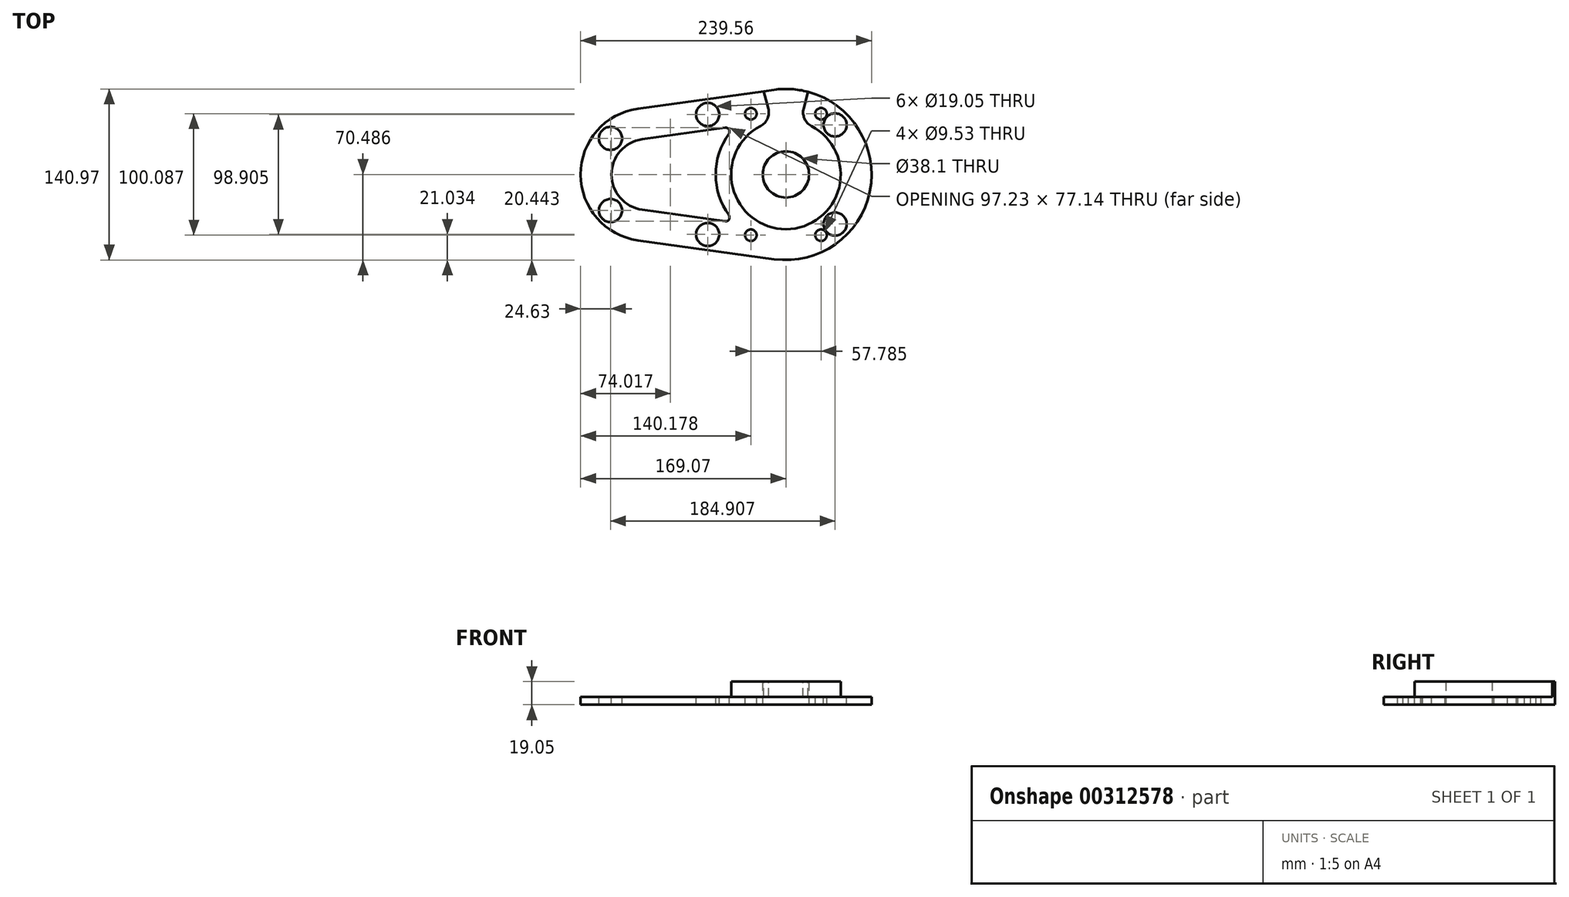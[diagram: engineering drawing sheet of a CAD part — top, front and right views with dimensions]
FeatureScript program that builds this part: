
annotation { "Feature Type Name" : "Feature", "Feature Type Description" : "" }
export const myFeature = defineFeature(function(context is Context, id is Id, definition is map)
    precondition{}
    {
        {
            var Q0;
            Q0=qCreatedBy(makeId("Top.planeOp"),FACE);
            var sketch = newSketch(context, id + "F0", { "sketchPlane" : qUnion([Q0])});
            skLineSegment(sketch, "E0", {"start": v(145.58, -278.48) * mm, "end": v(-159.22, -278.48) * mm});
            skLineSegment(sketch, "E1", {"start": v(-159.22, -278.48) * mm, "end": v(-159.22, -532.48) * mm});
            skLineSegment(sketch, "E2", {"start": v(-159.22, -532.48) * mm, "end": v(145.58, -532.48) * mm});
            skLineSegment(sketch, "E3", {"start": v(145.58, -278.48) * mm, "end": v(145.58, -532.48) * mm});
            skLineSegment(sketch, "E4", {"start": v(145.58, -11.78) * mm, "end": v(145.58, -265.78) * mm});
            skLineSegment(sketch, "E5", {"start": v(-159.22, -265.78) * mm, "end": v(145.58, -265.78) * mm});
            skLineSegment(sketch, "E6", {"start": v(-159.22, -11.78) * mm, "end": v(-159.22, -265.78) * mm});
            skLineSegment(sketch, "E7", {"start": v(145.58, -11.78) * mm, "end": v(-159.22, -11.78) * mm});
            skLineSegment(sketch, "E8", {"start": v(145.58, 254.92) * mm, "end": v(145.58, 0.92) * mm});
            skLineSegment(sketch, "E9", {"start": v(-159.22, 0.92) * mm, "end": v(145.58, 0.92) * mm});
            skLineSegment(sketch, "E10", {"start": v(-159.22, 254.92) * mm, "end": v(-159.22, 0.92) * mm});
            skLineSegment(sketch, "E11", {"start": v(145.58, 254.92) * mm, "end": v(-159.22, 254.92) * mm});
            skLineSegment(sketch, "E12", {"start": v(-79.36, -351.24) * mm, "end": v(32.78, -335.67) * mm});
            skArc(sketch, "E13", {"start": v(32.78, -335.67) * mm, "mid": v(112.96, -405.48) * mm, "end": v(32.78, -475.3) * mm});
            skLineSegment(sketch, "E14", {"start": v(32.78, -475.3) * mm, "end": v(-79.36, -459.73) * mm});
            skArc(sketch, "E15", {"start": v(-79.36, -459.73) * mm, "mid": v(-126.6, -405.48) * mm, "end": v(-79.36, -351.24) * mm});
            skArc(sketch, "E16", {"start": v(-75.87, -434.57) * mm, "mid": v(-101.2, -405.48) * mm, "end": v(-75.87, -376.4) * mm});
            skLineSegment(sketch, "E17", {"start": v(-75.87, -376.4) * mm, "end": v(-7.58, -366.91) * mm});
            skArc(sketch, "E18", {"start": v(-7.58, -366.91) * mm, "mid": v(-4.42, -368.41) * mm, "end": v(-4.56, -371.9) * mm});
            skArc(sketch, "E19", {"start": v(-4.56, -371.9) * mm, "mid": v(-15.31, -405.48) * mm, "end": v(-4.56, -439.06) * mm});
            skArc(sketch, "E20", {"start": v(-4.56, -439.06) * mm, "mid": v(-4.42, -442.55) * mm, "end": v(-7.58, -444.05) * mm});
            skLineSegment(sketch, "E21", {"start": v(-7.58, -444.05) * mm, "end": v(-75.87, -434.57) * mm});
            skArc(sketch, "E22", {"start": v(-36.82, 333.52) * mm, "mid": v(-66.33, 359.53) * mm, "end": v(-77.3, 397.3) * mm});
            skArc(sketch, "E23", {"start": v(-77.3, 397.3) * mm, "mid": v(-73.32, 420.67) * mm, "end": v(-61.81, 441.4) * mm});
            skArc(sketch, "E24", {"start": v(-61.81, 441.4) * mm, "mid": v(-58.7, 447) * mm, "end": v(-57.62, 453.32) * mm});
            skLineSegment(sketch, "E25", {"start": v(-57.62, 453.32) * mm, "end": v(-57.62, 486.2) * mm});
            skLineSegment(sketch, "E26", {"start": v(-57.62, 486.2) * mm, "end": v(43.98, 486.2) * mm});
            skLineSegment(sketch, "E27", {"start": v(43.98, 486.2) * mm, "end": v(43.98, 453.32) * mm});
            skArc(sketch, "E28", {"start": v(43.98, 453.32) * mm, "mid": v(45.06, 447) * mm, "end": v(48.17, 441.4) * mm});
            skArc(sketch, "E29", {"start": v(48.17, 441.4) * mm, "mid": v(59.68, 420.67) * mm, "end": v(63.66, 397.3) * mm});
            skArc(sketch, "E30", {"start": v(63.66, 397.3) * mm, "mid": v(52.69, 359.53) * mm, "end": v(23.17, 333.52) * mm});
            skArc(sketch, "E31", {"start": v(23.17, 333.52) * mm, "mid": v(15.2, 326.49) * mm, "end": v(12.23, 316.28) * mm});
            skLineSegment(sketch, "E32", {"start": v(12.23, 316.28) * mm, "end": v(12.23, 302.05) * mm});
            skArc(sketch, "E33", {"start": v(12.23, 302.05) * mm, "mid": v(10.37, 297.56) * mm, "end": v(5.88, 295.7) * mm});
            skLineSegment(sketch, "E34", {"start": v(5.88, 295.7) * mm, "end": v(-3.65, 295.7) * mm});
            skLineSegment(sketch, "E35", {"start": v(-3.65, 295.7) * mm, "end": v(-3.65, 352.33) * mm});
            skArc(sketch, "E36", {"start": v(-3.65, 352.33) * mm, "mid": v(7.85, 354.67) * mm, "end": v(18.36, 359.9) * mm});
            skArc(sketch, "E37", {"start": v(18.36, 359.9) * mm, "mid": v(20.05, 360.44) * mm, "end": v(21.77, 359.99) * mm});
            skArc(sketch, "E38", {"start": v(21.77, 359.99) * mm, "mid": v(29.55, 360.93) * mm, "end": v(30.5, 368.7) * mm});
            skArc(sketch, "E39", {"start": v(30.5, 368.7) * mm, "mid": v(30.04, 370.43) * mm, "end": v(30.58, 372.12) * mm});
            skArc(sketch, "E40", {"start": v(30.58, 372.12) * mm, "mid": v(38.26, 397.3) * mm, "end": v(30.58, 422.48) * mm});
            skArc(sketch, "E41", {"start": v(30.58, 422.48) * mm, "mid": v(30.04, 424.18) * mm, "end": v(30.5, 425.9) * mm});
            skArc(sketch, "E42", {"start": v(30.5, 425.9) * mm, "mid": v(29.55, 433.67) * mm, "end": v(21.77, 434.62) * mm});
            skArc(sketch, "E43", {"start": v(21.77, 434.62) * mm, "mid": v(20.05, 434.16) * mm, "end": v(18.36, 434.7) * mm});
            skArc(sketch, "E44", {"start": v(18.36, 434.7) * mm, "mid": v(-6.82, 442.39) * mm, "end": v(-32, 434.7) * mm});
            skArc(sketch, "E45", {"start": v(-32, 434.7) * mm, "mid": v(-33.7, 434.16) * mm, "end": v(-35.42, 434.62) * mm});
            skArc(sketch, "E46", {"start": v(-35.42, 434.62) * mm, "mid": v(-43.2, 433.67) * mm, "end": v(-44.14, 425.9) * mm});
            skArc(sketch, "E47", {"start": v(-44.14, 425.9) * mm, "mid": v(-43.68, 424.18) * mm, "end": v(-44.22, 422.48) * mm});
            skArc(sketch, "E48", {"start": v(-44.22, 422.48) * mm, "mid": v(-51.9, 397.3) * mm, "end": v(-44.22, 372.12) * mm});
            skArc(sketch, "E49", {"start": v(-44.22, 372.12) * mm, "mid": v(-43.68, 370.43) * mm, "end": v(-44.14, 368.7) * mm});
            skArc(sketch, "E50", {"start": v(-44.14, 368.7) * mm, "mid": v(-43.2, 360.93) * mm, "end": v(-35.42, 359.99) * mm});
            skArc(sketch, "E51", {"start": v(-35.42, 359.99) * mm, "mid": v(-33.7, 360.44) * mm, "end": v(-32, 359.9) * mm});
            skArc(sketch, "E52", {"start": v(-32, 359.9) * mm, "mid": v(-21.5, 354.67) * mm, "end": v(-10, 352.33) * mm});
            skLineSegment(sketch, "E53", {"start": v(-10, 352.33) * mm, "end": v(-10, 295.7) * mm});
            skLineSegment(sketch, "E54", {"start": v(-10, 295.7) * mm, "end": v(-19.52, 295.7) * mm});
            skArc(sketch, "E55", {"start": v(-19.52, 295.7) * mm, "mid": v(-24.01, 297.56) * mm, "end": v(-25.87, 302.05) * mm});
            skLineSegment(sketch, "E56", {"start": v(-25.87, 302.05) * mm, "end": v(-25.87, 316.28) * mm});
            skArc(sketch, "E57", {"start": v(-25.87, 316.28) * mm, "mid": v(-28.84, 326.49) * mm, "end": v(-36.82, 333.52) * mm});
            skLineSegment(sketch, "E58", {"start": v(-46.03, -68.97) * mm, "end": v(66.11, -84.54) * mm});
            skArc(sketch, "E59", {"start": v(66.11, -84.54) * mm, "mid": v(113.35, -138.78) * mm, "end": v(66.11, -193.03) * mm});
            skLineSegment(sketch, "E60", {"start": v(66.11, -193.03) * mm, "end": v(-46.03, -208.6) * mm});
            skArc(sketch, "E61", {"start": v(-46.03, -208.6) * mm, "mid": v(-126.2, -138.78) * mm, "end": v(-46.03, -68.97) * mm});
            skArc(sketch, "E62", {"start": v(63.42, -365.56) * mm, "mid": v(57.7, -359.41) * mm, "end": v(57.06, -351.03) * mm});
            skLineSegment(sketch, "E63", {"start": v(57.06, -351.03) * mm, "end": v(60.71, -337.4) * mm});
            skArc(sketch, "E64", {"start": v(60.71, -337.4) * mm, "mid": v(46.83, -335.13) * mm, "end": v(32.78, -335.67) * mm});
            skLineSegment(sketch, "E65", {"start": v(32.78, -335.67) * mm, "end": v(24.09, -336.87) * mm});
            skLineSegment(sketch, "E66", {"start": v(24.09, -336.87) * mm, "end": v(27.88, -351.03) * mm});
            skArc(sketch, "E67", {"start": v(27.88, -351.03) * mm, "mid": v(27.25, -359.41) * mm, "end": v(21.52, -365.56) * mm});
            skArc(sketch, "E68", {"start": v(21.52, -365.56) * mm, "mid": v(42.47, -450.57) * mm, "end": v(63.42, -365.56) * mm});
            skCircle(sketch, "E69", {"center": v(58.58, -138.78) * mm, "radius": 29.37 * mm});
            skCircle(sketch, "E70", {"center": v(42.47, -405.48) * mm, "radius": 19.05 * mm});
            skCircle(sketch, "E71", {"center": v(88.33, -109.04) * mm, "radius": 9.53 * mm});
            skCircle(sketch, "E72", {"center": v(8.3, -89.33) * mm, "radius": 9.53 * mm});
            skCircle(sketch, "E73", {"center": v(8.3, -188.24) * mm, "radius": 9.53 * mm});
            skCircle(sketch, "E74", {"center": v(-96.58, -97.92) * mm, "radius": 9.53 * mm});
            skCircle(sketch, "E75", {"center": v(-55.72, -138.78) * mm, "radius": 46.04 * mm});
            skCircle(sketch, "E76", {"center": v(88.33, -168.53) * mm, "radius": 9.53 * mm});
            skCircle(sketch, "E77", {"center": v(-96.58, -179.64) * mm, "radius": 9.53 * mm});
            skCircle(sketch, "E78", {"center": v(82.94, -364.62) * mm, "radius": 9.53 * mm});
            skCircle(sketch, "E79", {"center": v(-21.94, -356.03) * mm, "radius": 9.53 * mm});
            skCircle(sketch, "E80", {"center": v(-101.97, -375.74) * mm, "radius": 9.53 * mm});
            skCircle(sketch, "E81", {"center": v(-101.97, -435.23) * mm, "radius": 9.53 * mm});
            skCircle(sketch, "E82", {"center": v(-21.94, -454.94) * mm, "radius": 9.53 * mm});
            skCircle(sketch, "E83", {"center": v(82.94, -446.34) * mm, "radius": 9.53 * mm});
            skCircle(sketch, "E84", {"center": v(50.96, 397.3) * mm, "radius": 4.76 * mm});
            skCircle(sketch, "E85", {"center": v(-64.6, 397.3) * mm, "radius": 4.76 * mm});
            skCircle(sketch, "E86", {"center": v(71.36, -355.44) * mm, "radius": 4.76 * mm});
            skCircle(sketch, "E87", {"center": v(13.58, -455.53) * mm, "radius": 4.76 * mm});
            skCircle(sketch, "E88", {"center": v(13.58, -355.44) * mm, "radius": 4.76 * mm});
            skCircle(sketch, "E89", {"center": v(71.36, -455.53) * mm, "radius": 4.76 * mm});
            skCircle(sketch, "E90", {"center": v(-6.82, 127.92) * mm, "radius": 46.04 * mm});
            skCircle(sketch, "E91", {"center": v(-35.71, 77.87) * mm, "radius": 4.76 * mm});
            skCircle(sketch, "E92", {"center": v(22.07, 177.96) * mm, "radius": 4.76 * mm});
            skCircle(sketch, "E93", {"center": v(22.07, 77.87) * mm, "radius": 4.76 * mm});
            skCircle(sketch, "E94", {"center": v(-35.71, 177.96) * mm, "radius": 4.76 * mm});
            skCircle(sketch, "E95", {"center": v(-6.82, 127.92) * mm, "radius": 70.48 * mm});
            skCircle(sketch, "E96", {"center": v(-26.83, -88.74) * mm, "radius": 3.18 * mm});
            skCircle(sketch, "E97", {"center": v(-84.61, -88.74) * mm, "radius": 3.18 * mm});
            skCircle(sketch, "E98", {"center": v(-84.61, -188.83) * mm, "radius": 3.18 * mm});
            skCircle(sketch, "E99", {"center": v(-26.83, -188.83) * mm, "radius": 3.18 * mm});
            skSolve(sketch);
        }
        {
            var Q0;
            Q0=makeQuery(id+"F0.imprint","IMPRINT",FACE,{"disambiguationData":[TD([[makeQuery(id+"F0.imprint","IMPRINT",EDGE,{"derivedFrom":sQuery(id+"F0.wireOp",EDGE,"E12")}),-1.0]])]});
            var Q1;
            Q1=makeQuery(id+"F0.imprint","IMPRINT",FACE,{"disambiguationData":[TD([[makeQuery(id+"F0.imprint","IMPRINT",EDGE,{"derivedFrom":sQuery(id+"F0.wireOp",EDGE,"E62")}),1.0]])]});
            var Q2;
            Q2=makeQuery(id+"F0.imprint","IMPRINT",FACE,{"disambiguationData":[TD([[makeQuery(id+"F0.imprint","IMPRINT",EDGE,{"derivedFrom":sQuery(id+"F0.wireOp",EDGE,"E81")}),-1.0]])]});
            var Q3;
            Q3=makeQuery(id+"F0.imprint","IMPRINT",FACE,{"disambiguationData":[TD([[makeQuery(id+"F0.imprint","IMPRINT",EDGE,{"derivedFrom":sQuery(id+"F0.wireOp",EDGE,"E80")}),-1.0]])]});
            var Q4;
            Q4=makeQuery(id+"F0.imprint","IMPRINT",FACE,{"disambiguationData":[TD([[makeQuery(id+"F0.imprint","IMPRINT",EDGE,{"derivedFrom":sQuery(id+"F0.wireOp",EDGE,"E79")}),-1.0]])]});
            var Q5;
            Q5=makeQuery(id+"F0.imprint","IMPRINT",FACE,{"disambiguationData":[TD([[makeQuery(id+"F0.imprint","IMPRINT",EDGE,{"derivedFrom":sQuery(id+"F0.wireOp",EDGE,"E78")}),-1.0]])]});
            var Q6;
            Q6=makeQuery(id+"F0.imprint","IMPRINT",FACE,{"disambiguationData":[TD([[makeQuery(id+"F0.imprint","IMPRINT",EDGE,{"derivedFrom":sQuery(id+"F0.wireOp",EDGE,"E83")}),-1.0]])]});
            var Q7;
            Q7=makeQuery(id+"F0.imprint","IMPRINT",FACE,{"disambiguationData":[TD([[makeQuery(id+"F0.imprint","IMPRINT",EDGE,{"derivedFrom":sQuery(id+"F0.wireOp",EDGE,"E82")}),-1.0]])]});
            var Q8;
            Q8=makeQuery(id+"F0.imprint","IMPRINT",FACE,{"disambiguationData":[TD([[makeQuery(id+"F0.imprint","IMPRINT",EDGE,{"derivedFrom":sQuery(id+"F0.wireOp",EDGE,"E87")}),-1.0]])]});
            var Q9;
            Q9=makeQuery(id+"F0.imprint","IMPRINT",FACE,{"disambiguationData":[TD([[makeQuery(id+"F0.imprint","IMPRINT",EDGE,{"derivedFrom":sQuery(id+"F0.wireOp",EDGE,"E89")}),-1.0]])]});
            var Q10;
            Q10=makeQuery(id+"F0.imprint","IMPRINT",FACE,{"disambiguationData":[TD([[makeQuery(id+"F0.imprint","IMPRINT",EDGE,{"derivedFrom":sQuery(id+"F0.wireOp",EDGE,"E86")}),-1.0]])]});
            var Q11;
            Q11=makeQuery(id+"F0.imprint","IMPRINT",FACE,{"disambiguationData":[TD([[makeQuery(id+"F0.imprint","IMPRINT",EDGE,{"derivedFrom":sQuery(id+"F0.wireOp",EDGE,"E88")}),-1.0]])]});
            extrude(context, id + "F1", {"entities" : qUnion([Q0, Q1, Q2, Q3, Q4, Q5, Q6, Q7, Q8, Q9, Q10, Q11]), "oppositeDirection" : true, "depth" : 19.05 * mm});
        }
        {
            var Q0;
            Q0=makeQuery(id+"F0.imprint","IMPRINT",FACE,{"disambiguationData":[TD([[makeQuery(id+"F0.imprint","IMPRINT",EDGE,{"derivedFrom":sQuery(id+"F0.wireOp",EDGE,"E81")}),-1.0]])]});
            var Q1;
            Q1=makeQuery(id+"F0.imprint","IMPRINT",FACE,{"disambiguationData":[TD([[makeQuery(id+"F0.imprint","IMPRINT",EDGE,{"derivedFrom":sQuery(id+"F0.wireOp",EDGE,"E80")}),-1.0]])]});
            var Q2;
            Q2=makeQuery(id+"F0.imprint","IMPRINT",FACE,{"disambiguationData":[TD([[makeQuery(id+"F0.imprint","IMPRINT",EDGE,{"derivedFrom":sQuery(id+"F0.wireOp",EDGE,"E79")}),-1.0]])]});
            var Q3;
            Q3=makeQuery(id+"F0.imprint","IMPRINT",FACE,{"disambiguationData":[TD([[makeQuery(id+"F0.imprint","IMPRINT",EDGE,{"derivedFrom":sQuery(id+"F0.wireOp",EDGE,"E82")}),-1.0]])]});
            var Q4;
            Q4=makeQuery(id+"F0.imprint","IMPRINT",FACE,{"disambiguationData":[TD([[makeQuery(id+"F0.imprint","IMPRINT",EDGE,{"derivedFrom":sQuery(id+"F0.wireOp",EDGE,"E83")}),-1.0]])]});
            var Q5;
            Q5=makeQuery(id+"F0.imprint","IMPRINT",FACE,{"disambiguationData":[TD([[makeQuery(id+"F0.imprint","IMPRINT",EDGE,{"derivedFrom":sQuery(id+"F0.wireOp",EDGE,"E78")}),-1.0]])]});
            var Q6;
            Q6=makeQuery(id+"F0.imprint","IMPRINT",FACE,{"disambiguationData":[TD([[makeQuery(id+"F0.imprint","IMPRINT",EDGE,{"derivedFrom":sQuery(id+"F0.wireOp",EDGE,"E89")}),-1.0]])]});
            var Q7;
            Q7=makeQuery(id+"F0.imprint","IMPRINT",FACE,{"disambiguationData":[TD([[makeQuery(id+"F0.imprint","IMPRINT",EDGE,{"derivedFrom":sQuery(id+"F0.wireOp",EDGE,"E87")}),-1.0]])]});
            var Q8;
            Q8=makeQuery(id+"F0.imprint","IMPRINT",FACE,{"disambiguationData":[TD([[makeQuery(id+"F0.imprint","IMPRINT",EDGE,{"derivedFrom":sQuery(id+"F0.wireOp",EDGE,"E88")}),-1.0]])]});
            var Q9;
            Q9=makeQuery(id+"F0.imprint","IMPRINT",FACE,{"disambiguationData":[TD([[makeQuery(id+"F0.imprint","IMPRINT",EDGE,{"derivedFrom":sQuery(id+"F0.wireOp",EDGE,"E86")}),-1.0]])]});
            extrude(context, id + "F2", {"entities" : qUnion([Q0, Q1, Q2, Q3, Q4, Q5, Q6, Q7, Q8, Q9]), "operationType" : NewBodyOperationType.REMOVE, "oppositeDirection" : true, "depth" : 6.35 * mm});
        }
        {
            var Q0;
            Q0=makeQuery(id+"F0.imprint","IMPRINT",FACE,{"disambiguationData":[TD([[makeQuery(id+"F0.imprint","IMPRINT",EDGE,{"derivedFrom":sQuery(id+"F0.wireOp",EDGE,"E62")}),1.0]])]});
            extrude(context, id + "F3", {"entities" : qUnion([Q0]), "operationType" : NewBodyOperationType.REMOVE, "oppositeDirection" : true, "depth" : 12.7 * mm});
        }
    });
